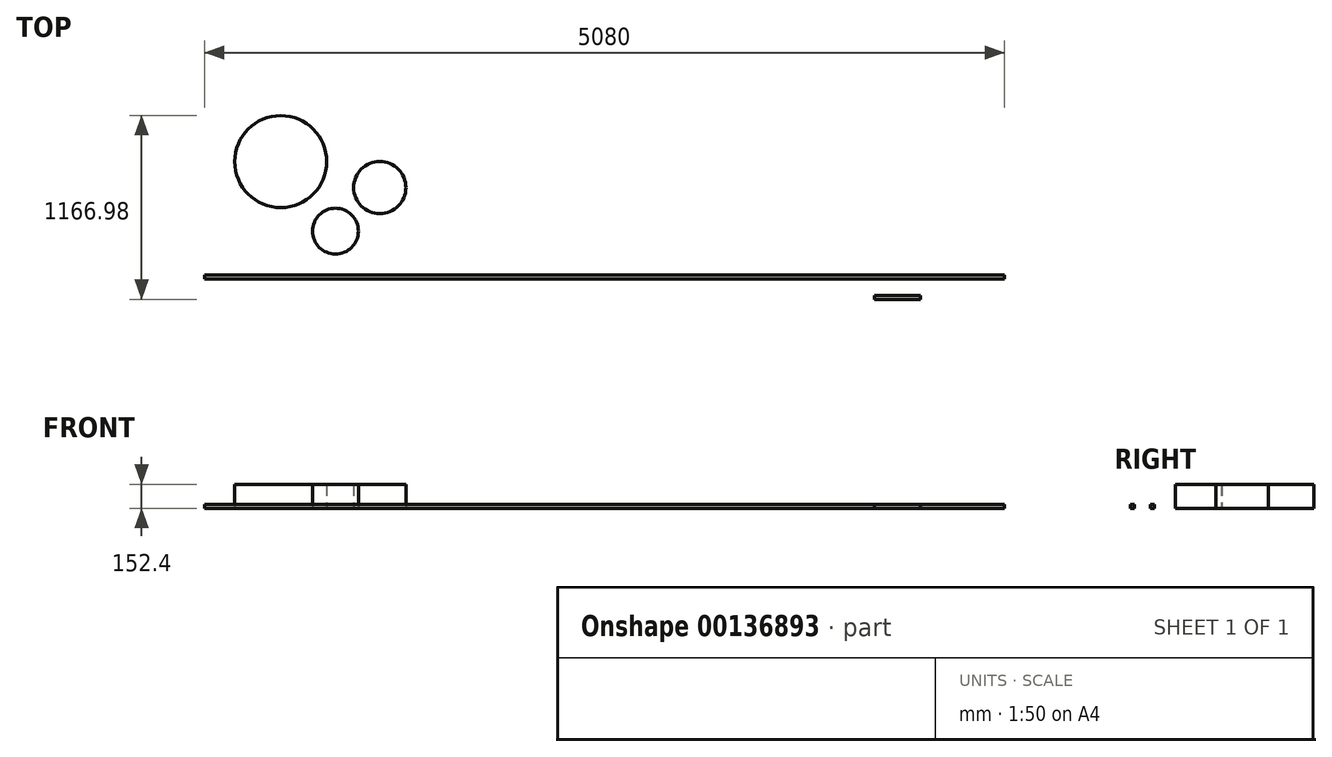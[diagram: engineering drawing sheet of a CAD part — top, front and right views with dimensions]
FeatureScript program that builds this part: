
annotation { "Feature Type Name" : "Feature", "Feature Type Description" : "" }
export const myFeature = defineFeature(function(context is Context, id is Id, definition is map)
    precondition{}
    {
        {
            var Q0;
            Q0=qCreatedBy(makeId("Top.planeOp"),FACE);
            var sketch = newSketch(context, id + "F0", { "sketchPlane" : qUnion([Q0])});
            skCircle(sketch, "E0", {"center": v(406.8, 0) * mm, "radius": 165.74 * mm});
            skSolve(sketch);
        }
        {
            var Q0;
            Q0=makeQuery(id+"F0.imprint","IMPRINT",FACE,{"disambiguationData":[TD([[makeQuery(id+"F0.imprint","IMPRINT",EDGE,{"derivedFrom":sQuery(id+"F0.wireOp",EDGE,"E0")}),1.0]])]});
            extrude(context, id + "F1", {"entities" : qUnion([Q0]), "depth" : 152.4 * mm});
        }
        {
            var Q0;
            Q0=qCreatedBy(makeId("Top.planeOp"),FACE);
            var sketch = newSketch(context, id + "F2", { "sketchPlane" : qUnion([Q0])});
            skCircle(sketch, "E1", {"center": v(125.43, -276.63) * mm, "radius": 145.54 * mm});
            skSolve(sketch);
        }
        {
            var Q0;
            Q0=makeQuery(id+"F2.imprint","IMPRINT",FACE,{"disambiguationData":[TD([[makeQuery(id+"F2.imprint","IMPRINT",EDGE,{"derivedFrom":sQuery(id+"F2.wireOp",EDGE,"E1")}),1.0]])]});
            extrude(context, id + "F3", {"entities" : qUnion([Q0]), "depth" : 152.4 * mm});
        }
        {
            var Q0;
            Q0=qCreatedBy(makeId("Top.planeOp"),FACE);
            var sketch = newSketch(context, id + "F4", { "sketchPlane" : qUnion([Q0])});
            skCircle(sketch, "E2", {"center": v(-222.07, 165.1) * mm, "radius": 292.1 * mm});
            skSolve(sketch);
        }
        {
            var Q0;
            Q0=makeQuery(id+"F4.imprint","IMPRINT",FACE,{"disambiguationData":[TD([[makeQuery(id+"F4.imprint","IMPRINT",EDGE,{"derivedFrom":sQuery(id+"F4.wireOp",EDGE,"E2")}),1.0]])]});
            extrude(context, id + "F5", {"entities" : qUnion([Q0]), "depth" : 152.4 * mm});
        }
        {
            var Q0;
            Q0=qCreatedBy(makeId("Top.planeOp"),FACE);
            var sketch = newSketch(context, id + "F6", { "sketchPlane" : qUnion([Q0])});
            skLineSegment(sketch, "E3.bottom", {"start": v(-705.98, -556.37) * mm, "end": v(4374.02, -556.37) * mm});
            skLineSegment(sketch, "E3.top", {"start": v(-705.98, -581.77) * mm, "end": v(4374.02, -581.77) * mm});
            skLineSegment(sketch, "E3.left", {"start": v(-705.98, -556.37) * mm, "end": v(-705.98, -581.77) * mm});
            skLineSegment(sketch, "E3.right", {"start": v(4374.02, -556.37) * mm, "end": v(4374.02, -581.77) * mm});
            skLineSegment(sketch, "E4.bottom", {"start": v(-121.78, -581.77) * mm, "end": v(-96.38, -581.77) * mm});
            skLineSegment(sketch, "E4.top", {"start": v(-121.78, -1165.97) * mm, "end": v(-96.38, -1165.97) * mm});
            skLineSegment(sketch, "E4.left", {"start": v(-121.78, -581.77) * mm, "end": v(-121.78, -1165.97) * mm});
            skLineSegment(sketch, "E4.right", {"start": v(-96.38, -581.77) * mm, "end": v(-96.38, -1165.97) * mm});
            skLineSegment(sketch, "E5.bottom", {"start": v(3027.82, -581.77) * mm, "end": v(3053.22, -581.77) * mm});
            skLineSegment(sketch, "E5.top", {"start": v(3027.82, -913.24) * mm, "end": v(3053.22, -913.24) * mm});
            skLineSegment(sketch, "E5.left", {"start": v(3027.82, -581.77) * mm, "end": v(3027.82, -913.24) * mm});
            skLineSegment(sketch, "E5.right", {"start": v(3053.22, -581.77) * mm, "end": v(3053.22, -913.24) * mm});
            skLineSegment(sketch, "E6.bottom", {"start": v(3384.69, -581.77) * mm, "end": v(3410.09, -581.77) * mm});
            skLineSegment(sketch, "E6.top", {"start": v(3384.69, -913.24) * mm, "end": v(3410.09, -913.24) * mm});
            skLineSegment(sketch, "E6.left", {"start": v(3384.69, -581.77) * mm, "end": v(3384.69, -913.24) * mm});
            skLineSegment(sketch, "E6.right", {"start": v(3410.09, -581.77) * mm, "end": v(3410.09, -913.24) * mm});
            skLineSegment(sketch, "E7.bottom", {"start": v(3524.39, -581.77) * mm, "end": v(3549.79, -581.77) * mm});
            skLineSegment(sketch, "E7.top", {"start": v(3524.39, -1000.87) * mm, "end": v(3549.79, -1000.87) * mm});
            skLineSegment(sketch, "E7.left", {"start": v(3524.39, -581.77) * mm, "end": v(3524.39, -1000.87) * mm});
            skLineSegment(sketch, "E7.right", {"start": v(3549.79, -581.77) * mm, "end": v(3549.79, -1000.87) * mm});
            skLineSegment(sketch, "E8.bottom", {"start": v(3549.79, -709.79) * mm, "end": v(3840.87, -709.79) * mm});
            skLineSegment(sketch, "E8.top", {"start": v(3549.79, -684.39) * mm, "end": v(3840.87, -684.39) * mm});
            skLineSegment(sketch, "E8.left", {"start": v(3549.79, -709.79) * mm, "end": v(3549.79, -684.39) * mm});
            skLineSegment(sketch, "E8.right", {"start": v(3840.87, -709.79) * mm, "end": v(3840.87, -684.39) * mm});
            skSolve(sketch);
        }
        {
            var Q0;
            Q0=makeQuery(id+"F6.imprint","IMPRINT",FACE,{"disambiguationData":[TD([[makeQuery(id+"F6.imprint","IMPRINT",EDGE,{"derivedFrom":sQuery(id+"F6.wireOp",EDGE,"E3.bottom")}),-1.0]])]});
            var Q1;
            Q1=makeQuery(id+"F6.imprint","IMPRINT",FACE,{"disambiguationData":[TD([[makeQuery(id+"F6.imprint","IMPRINT",EDGE,{"derivedFrom":sQuery(id+"F6.wireOp",EDGE,"E4.bottom")}),-1.0]])]});
            var Q2;
            Q2=makeQuery(id+"F6.imprint","IMPRINT",FACE,{"disambiguationData":[TD([[makeQuery(id+"F6.imprint","IMPRINT",EDGE,{"derivedFrom":sQuery(id+"F6.wireOp",EDGE,"E8.bottom")}),1.0]])]});
            var Q3;
            {var subQ1=sQuery(id+"F6.wireOp",EDGE,"E7.bottom");Q3=makeQuery(id+"F6.imprint","IMPRINT",FACE,{"disambiguationData":[TD([[makeQuery(id+"F6.imprint","IMPRINT",EDGE,{"derivedFrom":subQ1}),-1.0]])]});}
            var Q4;
            Q4=makeQuery(id+"F6.imprint","IMPRINT",FACE,{"disambiguationData":[TD([[makeQuery(id+"F6.imprint","IMPRINT",EDGE,{"derivedFrom":sQuery(id+"F6.wireOp",EDGE,"E6.bottom")}),-1.0]])]});
            var Q5;
            Q5=makeQuery(id+"F6.imprint","IMPRINT",FACE,{"disambiguationData":[TD([[makeQuery(id+"F6.imprint","IMPRINT",EDGE,{"derivedFrom":sQuery(id+"F6.wireOp",EDGE,"E5.bottom")}),-1.0]])]});
            extrude(context, id + "F7", {"entities" : qUnion([Q0, Q1, Q2, Q3, Q4, Q5]), "depth" : 25.4 * mm});
        }
    });
